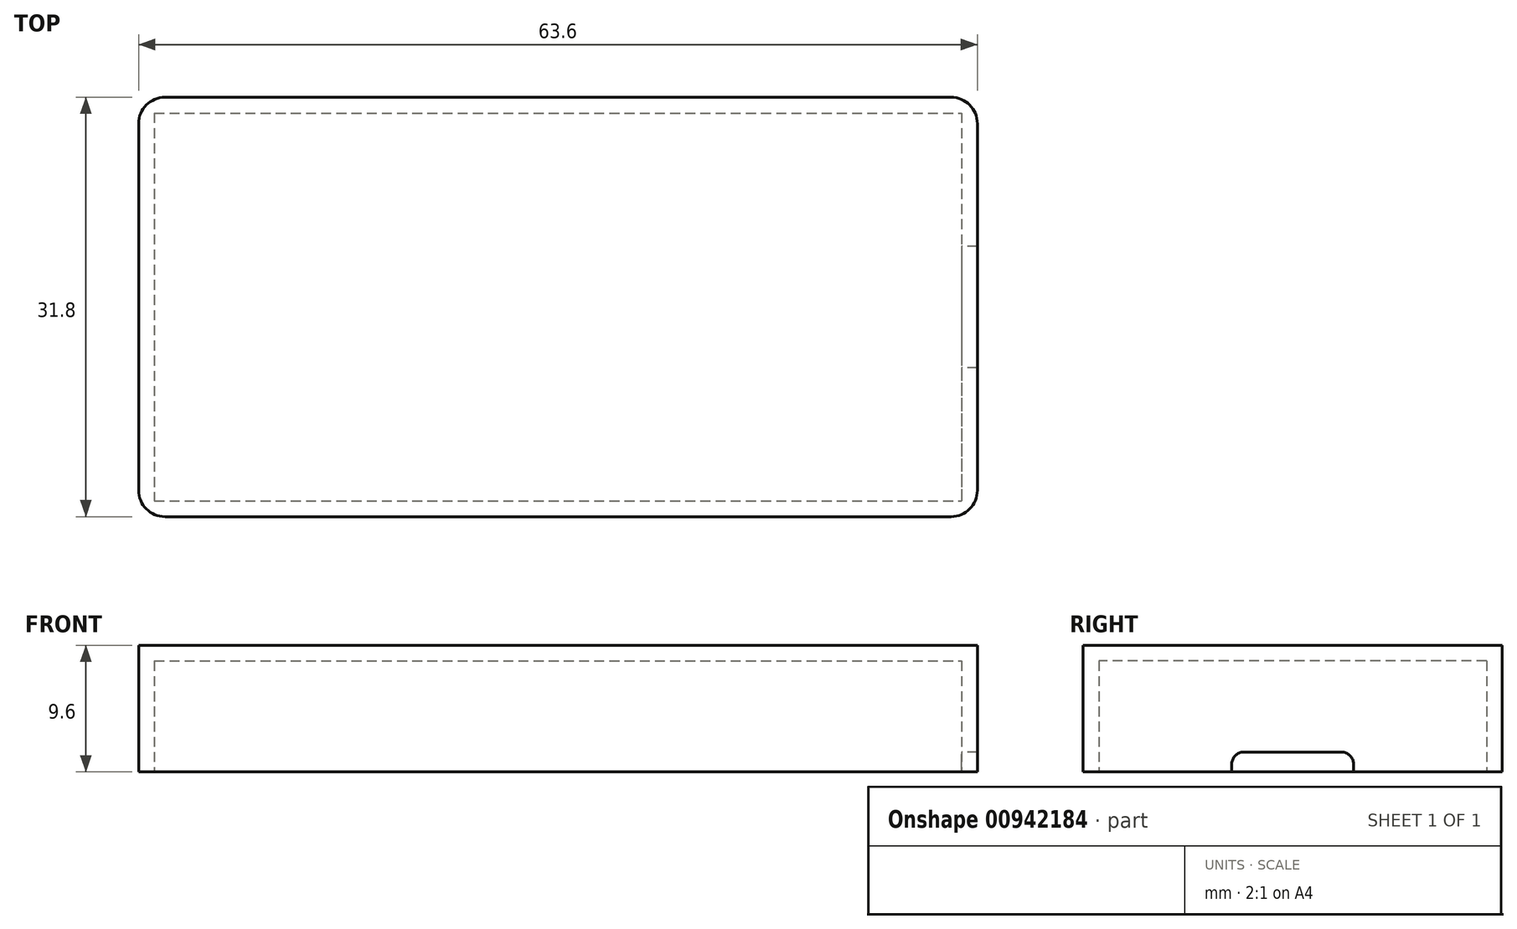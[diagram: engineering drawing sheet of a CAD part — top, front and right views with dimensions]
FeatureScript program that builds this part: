
annotation { "Feature Type Name" : "Feature", "Feature Type Description" : "" }
export const myFeature = defineFeature(function(context is Context, id is Id, definition is map)
    precondition{}
    {
        {
            var Q0;
            Q0=qCreatedBy(makeId("Top.planeOp"),FACE);
            var sketch = newSketch(context, id + "F0", { "sketchPlane" : qUnion([Q0])});
            skLineSegment(sketch, "E0.bottom", {"start": v(-31.8, 15.9) * mm, "end": v(31.8, 15.9) * mm});
            skLineSegment(sketch, "E0.top", {"start": v(-31.8, -15.9) * mm, "end": v(31.8, -15.9) * mm});
            skLineSegment(sketch, "E0.left", {"start": v(-31.8, 15.9) * mm, "end": v(-31.8, -15.9) * mm});
            skLineSegment(sketch, "E0.right", {"start": v(31.8, 15.9) * mm, "end": v(31.8, -15.9) * mm});
            skSolve(sketch);
        }
        {
            var Q0;
            Q0=qSketchRegion(id+"F0",true);
            extrude(context, id + "F1", {"entities" : qUnion([Q0]), "depth" : 9.6 * mm, "offsetDistance" : 25 * mm});
        }
        {
            var Q0;
            Q0=qCreatedBy(makeId("Top.planeOp"),FACE);
            var sketch = newSketch(context, id + "F2", { "sketchPlane" : qUnion([Q0])});
            skLineSegment(sketch, "E1.bottom", {"start": v(-30.6, 14.7) * mm, "end": v(30.6, 14.7) * mm});
            skLineSegment(sketch, "E1.top", {"start": v(-30.6, -14.7) * mm, "end": v(30.6, -14.7) * mm});
            skLineSegment(sketch, "E1.left", {"start": v(-30.6, 14.7) * mm, "end": v(-30.6, -14.7) * mm});
            skLineSegment(sketch, "E1.right", {"start": v(30.6, 14.7) * mm, "end": v(30.6, -14.7) * mm});
            skSolve(sketch);
        }
        {
            var Q0;
            Q0=qSketchRegion(id+"F2",true);
            extrude(context, id + "F3", {"entities" : qUnion([Q0]), "operationType" : NewBodyOperationType.REMOVE, "depth" : 8.4 * mm, "offsetDistance" : 25 * mm});
        }
        {
            var Q0;
            Q0=makeQuery(id+"F1.opExtrude","SWEPT_EDGE",EDGE,{"disambiguationData":[OSD([sQuery(id+"F0.wireOp",EDGE,"E0.top"),sQuery(id+"F0.wireOp",EDGE,"E0.left")])]});
            var Q1;
            Q1=makeQuery(id+"F1.opExtrude","SWEPT_EDGE",EDGE,{"disambiguationData":[OSD([sQuery(id+"F0.wireOp",EDGE,"E0.bottom"),sQuery(id+"F0.wireOp",EDGE,"E0.left")])]});
            var Q2;
            Q2=makeQuery(id+"F1.opExtrude","SWEPT_EDGE",EDGE,{"disambiguationData":[OSD([sQuery(id+"F0.wireOp",EDGE,"E0.bottom"),sQuery(id+"F0.wireOp",EDGE,"E0.right")])]});
            var Q3;
            Q3=makeQuery(id+"F1.opExtrude","SWEPT_EDGE",EDGE,{"disambiguationData":[OSD([sQuery(id+"F0.wireOp",EDGE,"E0.top"),sQuery(id+"F0.wireOp",EDGE,"E0.right")])]});
            fillet(context, id + "F4", {"entities" : qUnion([Q0, Q1, Q2, Q3]), "radius" : 2 * mm, "tangentPropagation" : true, "allowEdgeOverflow" : false});
        }
        {
            var Q0;
            Q0=qCreatedBy(makeId("Right.planeOp"),FACE);
            var sketch = newSketch(context, id + "F5", { "sketchPlane" : qUnion([Q0])});
            skLineSegment(sketch, "E2.bottom", {"start": v(-3.71, 1.5) * mm, "end": v(3.71, 1.5) * mm});
            skLineSegment(sketch, "E2.top", {"start": v(-3.71, -1.5) * mm, "end": v(3.71, -1.5) * mm});
            skLineSegment(sketch, "E2.left", {"start": v(-4.61, 0.6) * mm, "end": v(-4.61, -0.6) * mm});
            skLineSegment(sketch, "E2.right", {"start": v(4.61, 0.6) * mm, "end": v(4.61, -0.6) * mm});
            skPoint(sketch, "E2.middle", {"position": v(0, 0) * mm});
            skPoint(sketch, "E3", {"position": v(-3.71, 0.6) * mm});
            skPoint(sketch, "E4", {"position": v(3.71, 0.6) * mm});
            skPoint(sketch, "E5", {"position": v(3.71, -0.6) * mm});
            skPoint(sketch, "E6", {"position": v(-3.71, -0.6) * mm});
            skArc(sketch, "E7", {"start": v(-3.71, 1.5) * mm, "mid": v(-4.35, 1.24) * mm, "end": v(-4.61, 0.6) * mm});
            skArc(sketch, "E8", {"start": v(-4.61, -0.6) * mm, "mid": v(-4.35, -1.24) * mm, "end": v(-3.71, -1.5) * mm});
            skArc(sketch, "E9", {"start": v(3.71, -1.5) * mm, "mid": v(4.35, -1.24) * mm, "end": v(4.61, -0.6) * mm});
            skPoint(sketch, "E10.orphan", {"position": v(4.61, 1.5) * mm});
            skPoint(sketch, "E11.orphan", {"position": v(4.61, -1.5) * mm});
            skPoint(sketch, "E12.orphan", {"position": v(-4.61, -1.5) * mm});
            skPoint(sketch, "E13.orphan", {"position": v(-4.61, 1.5) * mm});
            skArc(sketch, "E14.trimOffspring", {"start": v(4.61, 0.6) * mm, "mid": v(4.35, 1.24) * mm, "end": v(3.71, 1.5) * mm});
            skSolve(sketch);
        }
        {
            var Q0;
            Q0 = qSketchRegion(id + "F5", true);
            extrude(context, id + "F6", {"entities" : qUnion([Q0]), "operationType" : NewBodyOperationType.REMOVE, "depth" : 32 * mm, "offsetDistance" : 25 * mm});
        }
    });
